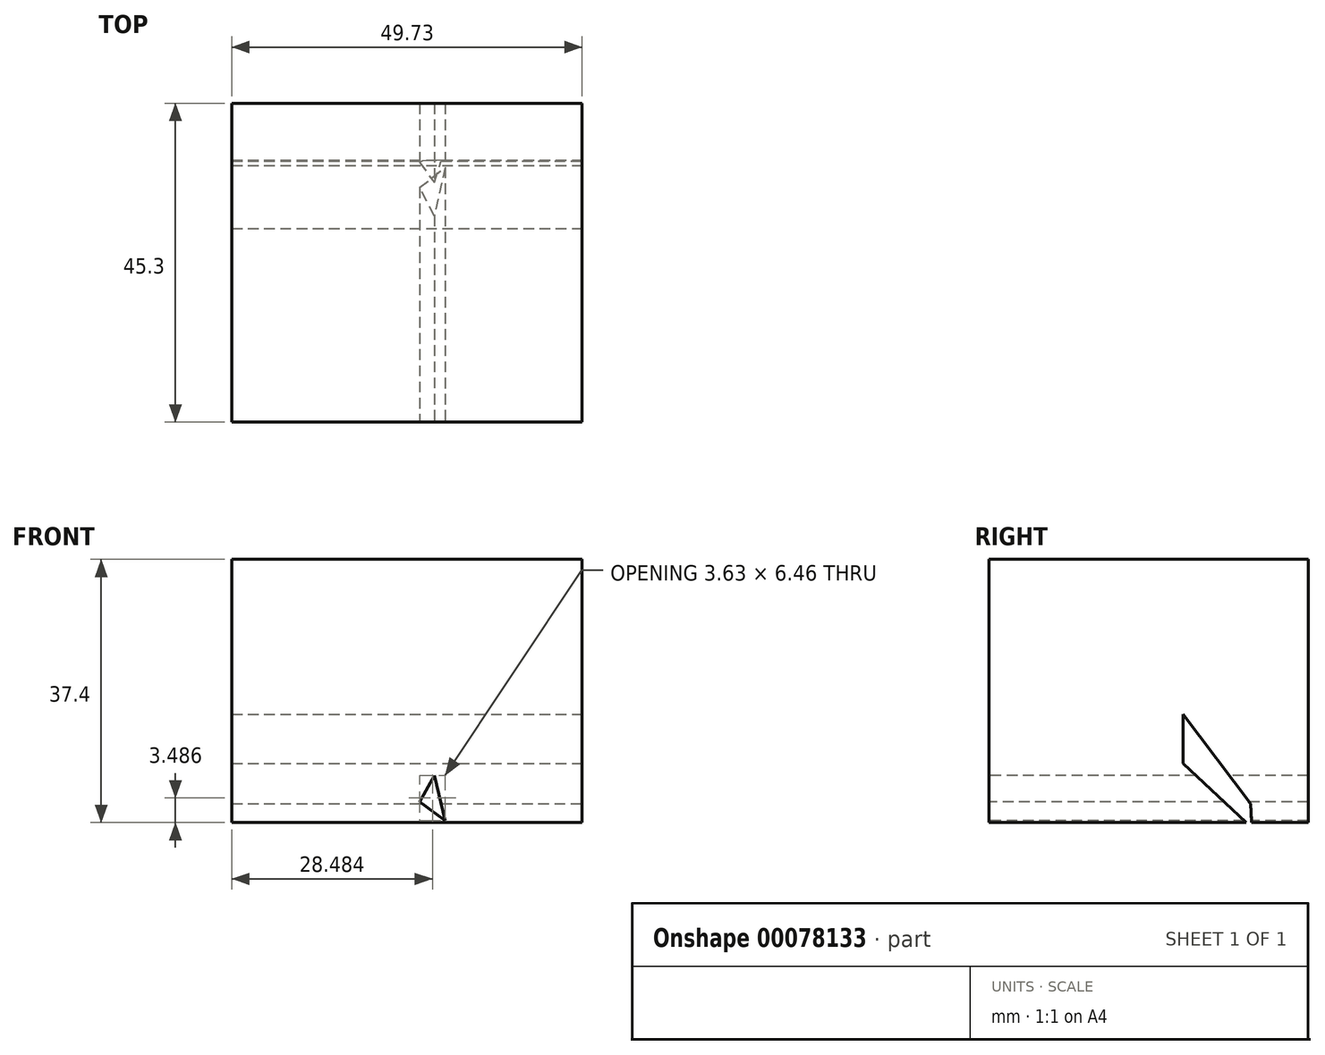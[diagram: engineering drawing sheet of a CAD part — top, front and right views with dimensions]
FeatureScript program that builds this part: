
annotation { "Feature Type Name" : "Feature", "Feature Type Description" : "" }
export const myFeature = defineFeature(function(context is Context, id is Id, definition is map)
    precondition{}
    {
        {
            var Q0;
            Q0=qCreatedBy(makeId("Top.planeOp"),FACE);
            var sketch = newSketch(context, id + "F0", { "sketchPlane" : qUnion([Q0])});
            skLineSegment(sketch, "E0.bottom", {"start": v(27.85, 28.14) * mm, "end": v(-21.88, 28.14) * mm});
            skLineSegment(sketch, "E0.top", {"start": v(27.85, -17.16) * mm, "end": v(-21.88, -17.16) * mm});
            skLineSegment(sketch, "E0.left", {"start": v(27.85, 28.14) * mm, "end": v(27.85, -17.16) * mm});
            skLineSegment(sketch, "E0.right", {"start": v(-21.88, 28.14) * mm, "end": v(-21.88, -17.16) * mm});
            skSolve(sketch);
        }
        {
            var Q0;
            Q0=makeQuery(id+"F0.imprint","IMPRINT",FACE,{"disambiguationData":[TD([[makeQuery(id+"F0.imprint","IMPRINT",EDGE,{"derivedFrom":sQuery(id+"F0.wireOp",EDGE,"E0.bottom")}),1.0]])]});
            extrude(context, id + "F1", {"entities" : qUnion([Q0]), "depth" : 25.4 * mm});
        }
        {
            var Q0;
            Q0=makeQuery(id+"F1.opExtrude","CAP_FACE",FACE,{"disambiguationData":[OSD([sQuery(id+"F0.wireOp",EDGE,"E0.bottom"),sQuery(id+"F0.wireOp",EDGE,"E0.top"),sQuery(id+"F0.wireOp",EDGE,"E0.left"),sQuery(id+"F0.wireOp",EDGE,"E0.right")])],"isStart":false});
            extrude(context, id + "F2", {"entities" : qUnion([Q0]), "operationType" : NewBodyOperationType.ADD, "depth" : 12 * mm});
        }
        {
            var Q0;
            Q0=makeQuery(id+"F2.opExtrude","CAP_FACE",FACE,{"disambiguationData":[OSD([sQuery(id+"F0.wireOp",EDGE,"E0.bottom"),sQuery(id+"F0.wireOp",EDGE,"E0.top"),sQuery(id+"F0.wireOp",EDGE,"E0.left"),sQuery(id+"F0.wireOp",EDGE,"E0.right")])],"isStart":false});
            var sketch = newSketch(context, id + "F3", { "sketchPlane" : qUnion([Q0])});
            skSolve(sketch);
        }
        {
            var Q0;
            {var subQ0=sQuery(id+"F0.wireOp",EDGE,"E0.left");Q0=makeQuery(id+"F2.boolean.opBoolean","MERGE",FACE,{"derivedFrom":[makeQuery(id+"F1.opExtrude","SWEPT_FACE",FACE,{"disambiguationData":[OSD([subQ0])]}),makeQuery(id+"F2.opExtrude","SWEPT_FACE",FACE,{"disambiguationData":[OSD([subQ0])]})]});}
            var sketch = newSketch(context, id + "F4", { "sketchPlane" : qUnion([Q0])});
            skLineSegment(sketch, "E1", {"start": v(10.38, 8.39) * mm, "end": v(10.38, 15.41) * mm});
            skLineSegment(sketch, "E2", {"start": v(10.38, 15.41) * mm, "end": v(19.94, 2.66) * mm});
            skLineSegment(sketch, "E3", {"start": v(19.94, 2.66) * mm, "end": v(20.13, -0.76) * mm});
            skLineSegment(sketch, "E4", {"start": v(20.13, -0.76) * mm, "end": v(10.38, 8.39) * mm});
            skSolve(sketch);
        }
        {
            var Q0;
            {var subQ5=sQuery(id+"F4.wireOp",EDGE,"E1");Q0=makeQuery(id+"F4.imprint","IMPRINT",FACE,{"disambiguationData":[TD([[makeQuery(id+"F4.imprint","IMPRINT",EDGE,{"derivedFrom":subQ5}),-1.0]])]});}
            extrude(context, id + "F5", {"entities" : qUnion([Q0]), "operationType" : NewBodyOperationType.REMOVE, "endBound" : BoundingType.THROUGH_ALL, "oppositeDirection" : true, "depth" : 25.4 * mm});
        }
        {
            var Q0;
            {var subQ0=sQuery(id+"F0.wireOp",EDGE,"E0.top");Q0=makeQuery(id+"F2.boolean.opBoolean","MERGE",FACE,{"derivedFrom":[makeQuery(id+"F1.opExtrude","SWEPT_FACE",FACE,{"disambiguationData":[OSD([subQ0])]}),makeQuery(id+"F2.opExtrude","SWEPT_FACE",FACE,{"disambiguationData":[OSD([subQ0])]})]});}
            var sketch = newSketch(context, id + "F6", { "sketchPlane" : qUnion([Q0])});
            skLineSegment(sketch, "E5", {"start": v(4.8, 2.94) * mm, "end": v(6.85, 6.71) * mm});
            skLineSegment(sketch, "E6", {"start": v(6.85, 6.71) * mm, "end": v(8.42, 0.26) * mm});
            skLineSegment(sketch, "E7", {"start": v(8.42, 0.26) * mm, "end": v(4.8, 2.94) * mm});
            skSolve(sketch);
        }
        {
            var Q0;
            Q0=makeQuery(id+"F6.imprint","IMPRINT",FACE,{"disambiguationData":[TD([[makeQuery(id+"F6.imprint","IMPRINT",EDGE,{"derivedFrom":sQuery(id+"F6.wireOp",EDGE,"E5")}),-1.0]])]});
            extrude(context, id + "F7", {"entities" : qUnion([Q0]), "operationType" : NewBodyOperationType.REMOVE, "endBound" : BoundingType.THROUGH_ALL, "oppositeDirection" : true, "depth" : 25.4 * mm});
        }
    });
